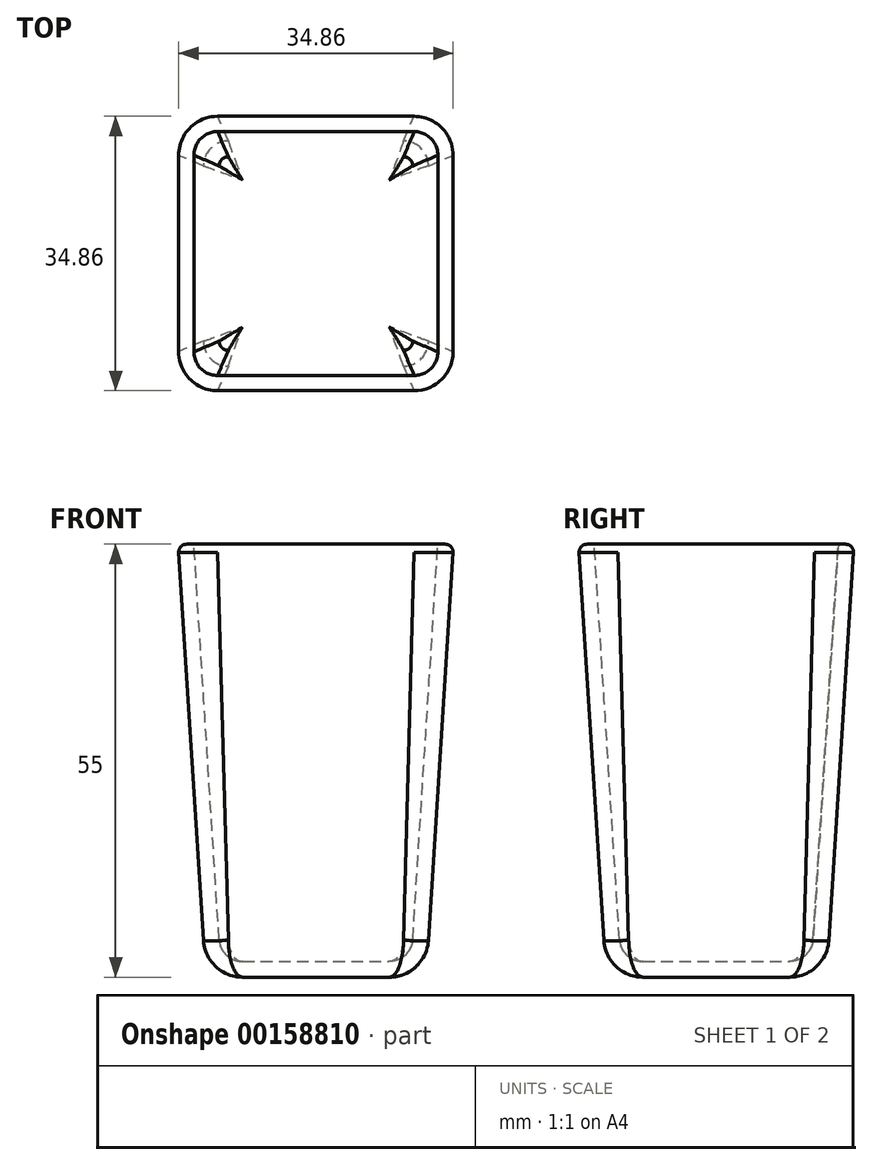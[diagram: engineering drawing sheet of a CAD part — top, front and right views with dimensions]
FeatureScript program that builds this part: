
annotation { "Feature Type Name" : "Feature", "Feature Type Description" : "" }
export const myFeature = defineFeature(function(context is Context, id is Id, definition is map)
    precondition{}
    {
        {
            var Q0;
            Q0=qCreatedBy(makeId("Top.planeOp"),FACE);
            var sketch = newSketch(context, id + "F0", { "sketchPlane" : qUnion([Q0])});
            skLineSegment(sketch, "E0.bottom", {"start": v(11, 14) * mm, "end": v(-11, 14) * mm});
            skLineSegment(sketch, "E0.top", {"start": v(11, -14) * mm, "end": v(-11, -14) * mm});
            skLineSegment(sketch, "E0.left", {"start": v(14, 11) * mm, "end": v(14, -11) * mm});
            skLineSegment(sketch, "E0.right", {"start": v(-14, 11) * mm, "end": v(-14, -11) * mm});
            skPoint(sketch, "E0.middle", {"position": v(0, 0) * mm});
            skPoint(sketch, "E1.visualSharp", {"position": v(-14, 14) * mm});
            skArc(sketch, "E1.filletArc", {"start": v(-11, 14) * mm, "mid": v(-13.12, 13.12) * mm, "end": v(-14, 11) * mm});
            skPoint(sketch, "E2.visualSharp", {"position": v(14, 14) * mm});
            skArc(sketch, "E2.filletArc", {"start": v(14, 11) * mm, "mid": v(13.12, 13.12) * mm, "end": v(11, 14) * mm});
            skPoint(sketch, "E3.visualSharp", {"position": v(14, -14) * mm});
            skArc(sketch, "E3.filletArc", {"start": v(11, -14) * mm, "mid": v(13.12, -13.12) * mm, "end": v(14, -11) * mm});
            skPoint(sketch, "E4.visualSharp", {"position": v(-14, -14) * mm});
            skArc(sketch, "E4.filletArc", {"start": v(-14, -11) * mm, "mid": v(-13.12, -13.12) * mm, "end": v(-11, -14) * mm});
            skSolve(sketch);
        }
        {
            var Q0;
            Q0=qCreatedBy(makeId("Top.planeOp"),FACE);
            cPlane(context, id + "F1", {"entities" : qUnion([Q0]), "cplaneType" : CPlaneType.OFFSET, "offset" : 55 * mm, "width" : 150 * mm, "height" : 150 * mm});
        }
        {
            var Q0;
            Q0=qCreatedBy(id+"F1.planeOp",FACE);
            var sketch = newSketch(context, id + "F2", { "sketchPlane" : qUnion([Q0])});
            skLineSegment(sketch, "E5.bottom", {"start": v(12.5, 17.5) * mm, "end": v(-12.5, 17.5) * mm});
            skLineSegment(sketch, "E5.top", {"start": v(12.5, -17.5) * mm, "end": v(-12.5, -17.5) * mm});
            skLineSegment(sketch, "E5.left", {"start": v(17.5, 12.5) * mm, "end": v(17.5, -12.5) * mm});
            skLineSegment(sketch, "E5.right", {"start": v(-17.5, 12.5) * mm, "end": v(-17.5, -12.5) * mm});
            skPoint(sketch, "E5.middle", {"position": v(0, 0) * mm});
            skPoint(sketch, "E6.visualSharp", {"position": v(-17.5, 17.5) * mm});
            skArc(sketch, "E6.filletArc", {"start": v(-12.5, 17.5) * mm, "mid": v(-16.04, 16.04) * mm, "end": v(-17.5, 12.5) * mm});
            skPoint(sketch, "E7.visualSharp", {"position": v(17.5, 17.5) * mm});
            skArc(sketch, "E7.filletArc", {"start": v(17.5, 12.5) * mm, "mid": v(16.04, 16.04) * mm, "end": v(12.5, 17.5) * mm});
            skPoint(sketch, "E8.visualSharp", {"position": v(17.5, -17.5) * mm});
            skArc(sketch, "E8.filletArc", {"start": v(12.5, -17.5) * mm, "mid": v(16.04, -16.04) * mm, "end": v(17.5, -12.5) * mm});
            skPoint(sketch, "E9.visualSharp", {"position": v(-17.5, -17.5) * mm});
            skArc(sketch, "E9.filletArc", {"start": v(-17.5, -12.5) * mm, "mid": v(-16.04, -16.04) * mm, "end": v(-12.5, -17.5) * mm});
            skSolve(sketch);
        }
        {
            var Q0;
            Q0=makeQuery(id+"F0.imprint","IMPRINT",FACE,{"disambiguationData":[TD([[makeQuery(id+"F0.imprint","IMPRINT",EDGE,{"derivedFrom":sQuery(id+"F0.wireOp",EDGE,"E0.bottom")}),1.0]])]});
            var Q1;
            Q1=makeQuery(id+"F2.imprint","IMPRINT",FACE,{"disambiguationData":[TD([[makeQuery(id+"F2.imprint","IMPRINT",EDGE,{"derivedFrom":sQuery(id+"F2.wireOp",EDGE,"E5.bottom")}),1.0]])]});
            loft(context, id + "F3", {"sheetProfilesArray" : [{ "sheetProfileEntities" : qUnion([Q0]) }, { "sheetProfileEntities" : qUnion([Q1]) }]});
        }
        {
            var Q0;
            Q0=makeQuery(id+"F3.opLoft","MID_CAP_EDGE",EDGE,{"disambiguationData":[OSD([sQuery(id+"F0.wireOp",EDGE,"E0.left"),sQuery(id+"F0.wireOp",EDGE,"E2.filletArc"),sQuery(id+"F0.wireOp",EDGE,"E3.filletArc")])],"capPos":0.0});
            fillet(context, id + "F4", {"entities" : qUnion([Q0]), "radius" : 5 * mm, "tangentPropagation" : true, "allowEdgeOverflow" : false});
        }
        {
            var Q0;
            Q0=makeQuery(id+"F3.opLoft","CAP_FACE",FACE,{"disambiguationData":[OSD([makeQuery(id+"F2.imprint","IMPRINT",FACE,{"disambiguationData":[TD([[makeQuery(id+"F2.imprint","IMPRINT",EDGE,{"derivedFrom":sQuery(id+"F2.wireOp",EDGE,"E5.bottom")}),1.0]])]})])],"isStart":true});
            shell(context, id + "F5", {"entities" : qUnion([Q0]), "thickness" : 2 * mm});
        }
        {
            var Q0;
            Q0=makeQuery(id+"F3.opLoft","MID_CAP_EDGE",EDGE,{"disambiguationData":[OSD([sQuery(id+"F2.wireOp",EDGE,"E5.top"),sQuery(id+"F2.wireOp",EDGE,"E8.filletArc"),sQuery(id+"F2.wireOp",EDGE,"E9.filletArc")])],"capPos":1.0});
            fillet(context, id + "F6", {"entities" : qUnion([Q0]), "radius" : 1 * mm, "tangentPropagation" : true, "allowEdgeOverflow" : false});
        }
    });
